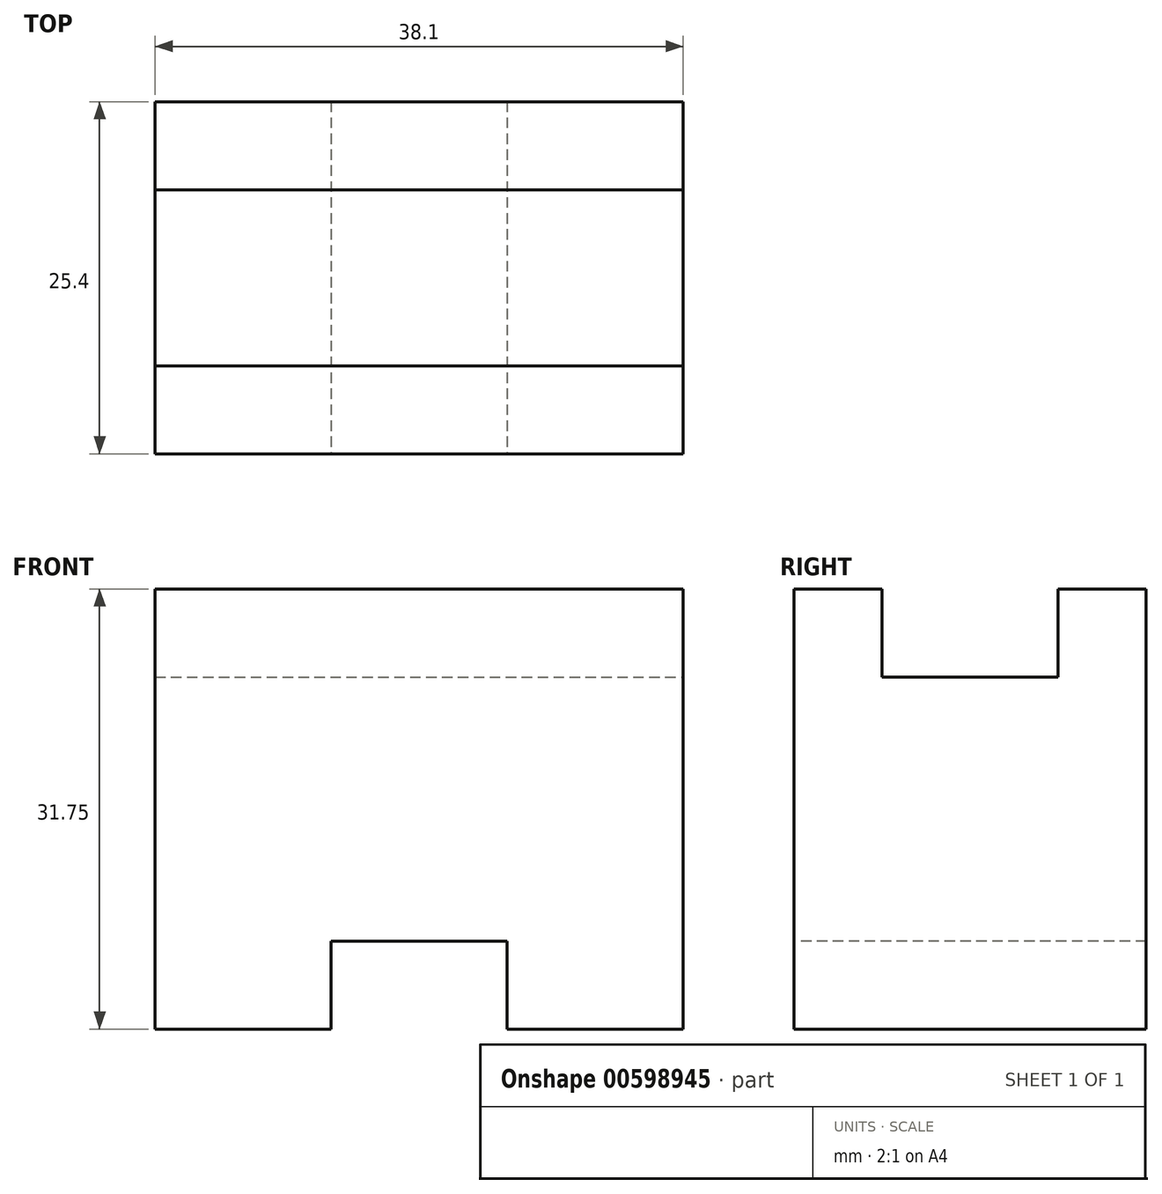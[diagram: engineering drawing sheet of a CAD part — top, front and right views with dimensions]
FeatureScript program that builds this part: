
annotation { "Feature Type Name" : "Feature", "Feature Type Description" : "" }
export const myFeature = defineFeature(function(context is Context, id is Id, definition is map)
    precondition{}
    {
        {
            var Q0;
            Q0=qCreatedBy(makeId("Front.planeOp"),FACE);
            var sketch = newSketch(context, id + "F0", { "sketchPlane" : qUnion([Q0])});
            skLineSegment(sketch, "E0", {"start": v(0, 0) * mm, "end": v(19.05, 0) * mm});
            skLineSegment(sketch, "E1", {"start": v(19.05, 0) * mm, "end": v(-19.05, 0) * mm});
            skLineSegment(sketch, "E2", {"start": v(-19.05, 0) * mm, "end": v(-19.05, -31.75) * mm});
            skLineSegment(sketch, "E3", {"start": v(-19.05, -31.75) * mm, "end": v(19.05, -31.75) * mm});
            skLineSegment(sketch, "E4", {"start": v(19.05, -31.75) * mm, "end": v(19.05, 0) * mm});
            skSolve(sketch);
        }
        {
            var Q0;
            Q0 = qSketchRegion(id + "F0", true);
            extrude(context, id + "F1", {"entities" : qUnion([Q0]), "depth" : 25.4 * mm, "offsetDistance" : 25.4 * mm});
        }
        {
            var Q0;
            Q0=makeQuery(id+"F1.opExtrude","CAP_FACE",FACE,{"disambiguationData":[OSD([sQuery(id+"F0.wireOp",EDGE,"E1"),sQuery(id+"F0.wireOp",EDGE,"E2"),sQuery(id+"F0.wireOp",EDGE,"E3"),sQuery(id+"F0.wireOp",EDGE,"E4")])],"isStart":false});
            var sketch = newSketch(context, id + "F2", { "sketchPlane" : qUnion([Q0])});
            skLineSegment(sketch, "E5", {"start": v(-6.35, -31.75) * mm, "end": v(6.35, -31.75) * mm});
            skLineSegment(sketch, "E6", {"start": v(6.35, -31.75) * mm, "end": v(6.35, -25.4) * mm});
            skLineSegment(sketch, "E7", {"start": v(6.35, -25.4) * mm, "end": v(-6.35, -25.4) * mm});
            skLineSegment(sketch, "E8", {"start": v(-6.35, -25.4) * mm, "end": v(-6.35, -31.75) * mm});
            skSolve(sketch);
        }
        {
            var Q0;
            Q0 = qSketchRegion(id + "F2", true);
            extrude(context, id + "F3", {"entities" : qUnion([Q0]), "operationType" : NewBodyOperationType.REMOVE, "oppositeDirection" : true, "depth" : 25.4 * mm, "offsetDistance" : 25.4 * mm});
        }
        {
            var Q0;
            Q0=makeQuery(id+"F1.opExtrude","SWEPT_FACE",FACE,{"disambiguationData":[OSD([sQuery(id+"F0.wireOp",EDGE,"E1")])]});
            var sketch = newSketch(context, id + "F4", { "sketchPlane" : qUnion([Q0])});
            skLineSegment(sketch, "E9", {"start": v(-19.05, -6.35) * mm, "end": v(19.05, -6.35) * mm});
            skLineSegment(sketch, "E10", {"start": v(19.05, -6.35) * mm, "end": v(19.05, -19.05) * mm});
            skLineSegment(sketch, "E11", {"start": v(19.05, -19.05) * mm, "end": v(-19.05, -19.05) * mm});
            skLineSegment(sketch, "E12", {"start": v(-19.05, -19.05) * mm, "end": v(-19.05, -6.35) * mm});
            skSolve(sketch);
        }
        {
            var Q0;
            Q0 = qSketchRegion(id + "F4", true);
            extrude(context, id + "F5", {"entities" : qUnion([Q0]), "operationType" : NewBodyOperationType.REMOVE, "oppositeDirection" : true, "depth" : 6.35 * mm, "offsetDistance" : 25.4 * mm});
        }
    });
